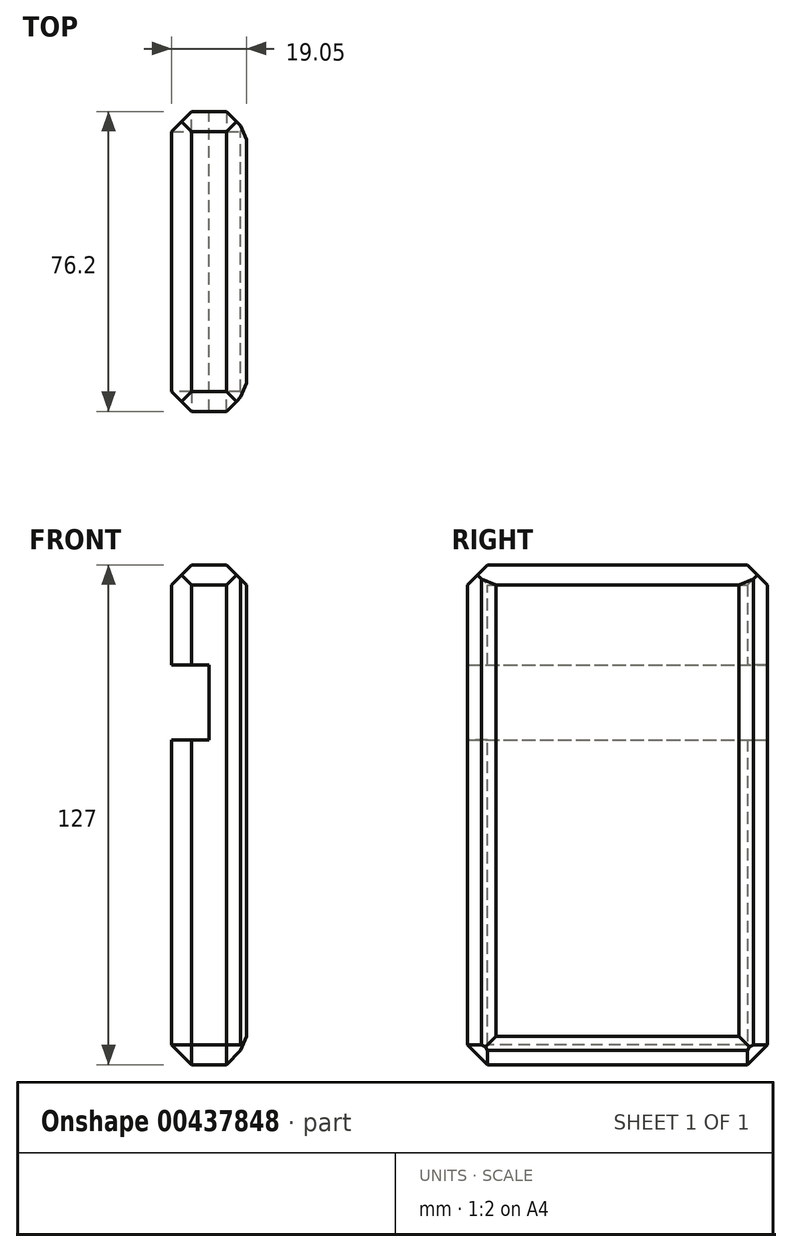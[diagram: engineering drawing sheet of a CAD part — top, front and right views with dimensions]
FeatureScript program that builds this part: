
annotation { "Feature Type Name" : "Feature", "Feature Type Description" : "" }
export const myFeature = defineFeature(function(context is Context, id is Id, definition is map)
    precondition{}
    {
        {
            var Q0;
            Q0=qCreatedBy(makeId("Front.planeOp"),FACE);
            var sketch = newSketch(context, id + "F0", { "sketchPlane" : qUnion([Q0])});
            skLineSegment(sketch, "E0", {"start": v(13.13, -19.14) * mm, "end": v(13.13, 107.86) * mm});
            skLineSegment(sketch, "E1", {"start": v(13.13, 107.86) * mm, "end": v(-5.92, 107.86) * mm});
            skLineSegment(sketch, "E2", {"start": v(-5.92, 107.86) * mm, "end": v(-5.92, 82.46) * mm});
            skLineSegment(sketch, "E3", {"start": v(-5.92, 82.46) * mm, "end": v(3.6, 82.46) * mm});
            skLineSegment(sketch, "E4", {"start": v(3.6, 82.46) * mm, "end": v(3.6, 63.41) * mm});
            skLineSegment(sketch, "E5", {"start": v(3.6, 63.41) * mm, "end": v(-5.92, 63.41) * mm});
            skLineSegment(sketch, "E6", {"start": v(-5.92, 63.41) * mm, "end": v(-5.92, -19.14) * mm});
            skLineSegment(sketch, "E7", {"start": v(-5.92, -19.14) * mm, "end": v(13.13, -19.14) * mm});
            skSolve(sketch);
        }
        {
            var Q0;
            Q0 = qSketchRegion(id + "F0", true);
            extrude(context, id + "F1", {"entities" : qUnion([Q0]), "depth" : 76.2 * mm});
        }
        {
            var Q0;
            Q0=makeQuery(id+"F1.opExtrude","CAP_EDGE",EDGE,{"disambiguationData":[OSD([sQuery(id+"F0.wireOp",EDGE,"E2")])],"isStart":true});
            var Q1;
            Q1=makeQuery(id+"F1.opExtrude","CAP_EDGE",EDGE,{"disambiguationData":[OSD([sQuery(id+"F0.wireOp",EDGE,"E0")])],"isStart":true});
            var Q2;
            Q2=makeQuery(id+"F1.opExtrude","CAP_EDGE",EDGE,{"disambiguationData":[OSD([sQuery(id+"F0.wireOp",EDGE,"E7")])],"isStart":true});
            var Q3;
            Q3=makeQuery(id+"F1.opExtrude","CAP_EDGE",EDGE,{"disambiguationData":[OSD([sQuery(id+"F0.wireOp",EDGE,"E6")])],"isStart":true});
            var Q4;
            Q4=makeQuery(id+"F1.opExtrude","SWEPT_EDGE",EDGE,{"disambiguationData":[OSD([sQuery(id+"F0.wireOp",EDGE,"E6"),sQuery(id+"F0.wireOp",EDGE,"E7")])]});
            var Q5;
            Q5=makeQuery(id+"F1.opExtrude","CAP_EDGE",EDGE,{"disambiguationData":[OSD([sQuery(id+"F0.wireOp",EDGE,"E6")])],"isStart":false});
            var Q6;
            Q6=makeQuery(id+"F1.opExtrude","SWEPT_EDGE",EDGE,{"disambiguationData":[OSD([sQuery(id+"F0.wireOp",EDGE,"E0"),sQuery(id+"F0.wireOp",EDGE,"E7")])]});
            var Q7;
            Q7=makeQuery(id+"F1.opExtrude","CAP_EDGE",EDGE,{"disambiguationData":[OSD([sQuery(id+"F0.wireOp",EDGE,"E7")])],"isStart":false});
            var Q8;
            Q8=makeQuery(id+"F1.opExtrude","CAP_EDGE",EDGE,{"disambiguationData":[OSD([sQuery(id+"F0.wireOp",EDGE,"E0")])],"isStart":false});
            var Q9;
            Q9=makeQuery(id+"F1.opExtrude","CAP_EDGE",EDGE,{"disambiguationData":[OSD([sQuery(id+"F0.wireOp",EDGE,"E1")])],"isStart":false});
            var Q10;
            Q10=makeQuery(id+"F1.opExtrude","SWEPT_EDGE",EDGE,{"disambiguationData":[OSD([sQuery(id+"F0.wireOp",EDGE,"E1"),sQuery(id+"F0.wireOp",EDGE,"E2")])]});
            chamfer(context, id + "F2", {"entities" : qUnion([Q0, Q1, Q2, Q3, Q4, Q5, Q6, Q7, Q8, Q9, Q10]), "width" : 5.08 * mm, "tangentPropagation" : true});
        }
        {
            var Q0;
            Q0=makeQuery(id+"F1.opExtrude","CAP_EDGE",EDGE,{"disambiguationData":[OSD([sQuery(id+"F0.wireOp",EDGE,"E2")])],"isStart":false});
            chamfer(context, id + "F3", {"entities" : qUnion([Q0]), "width" : 5.08 * mm, "tangentPropagation" : true});
        }
        {
            var Q0;
            Q0=makeQuery(id+"F1.opExtrude","CAP_EDGE",EDGE,{"disambiguationData":[OSD([sQuery(id+"F0.wireOp",EDGE,"E1")])],"isStart":true});
            chamfer(context, id + "F4", {"entities" : qUnion([Q0]), "width" : 5.08 * mm, "tangentPropagation" : true});
        }
        {
            var Q0;
            Q0=makeQuery(id+"F1.opExtrude","SWEPT_EDGE",EDGE,{"disambiguationData":[OSD([sQuery(id+"F0.wireOp",EDGE,"E0"),sQuery(id+"F0.wireOp",EDGE,"E1")])]});
            var Q1;
            {var subQ0=sQuery(id+"F0.wireOp",EDGE,"E0");Q1=makeQuery(id+"F2.opChamfer","BLEND_EDGE",EDGE,{"blendedFrom":[makeQuery(id+"F1.opExtrude","CAP_EDGE",EDGE,{"disambiguationData":[OSD([subQ0])],"isStart":false}),makeQuery(id+"F1.opExtrude","SWEPT_FACE",FACE,{"disambiguationData":[OSD([subQ0])]})],"blendedInto":[makeQuery(id+"F1.opExtrude","SWEPT_FACE",FACE,{"disambiguationData":[OSD([subQ0])]})]});}
            var Q2;
            {var subQ0=sQuery(id+"F0.wireOp",EDGE,"E0");Q2=makeQuery(id+"F2.opChamfer","BLEND_EDGE",EDGE,{"blendedFrom":[makeQuery(id+"F1.opExtrude","CAP_EDGE",EDGE,{"disambiguationData":[OSD([subQ0])],"isStart":true}),makeQuery(id+"F1.opExtrude","SWEPT_FACE",FACE,{"disambiguationData":[OSD([subQ0])]})],"blendedInto":[makeQuery(id+"F1.opExtrude","SWEPT_FACE",FACE,{"disambiguationData":[OSD([subQ0])]})]});}
            var Q3;
            {var subQ0=sQuery(id+"F0.wireOp",EDGE,"E0");Q3=makeQuery(id+"F2.opChamfer","BLEND_EDGE",EDGE,{"blendedFrom":[makeQuery(id+"F1.opExtrude","SWEPT_EDGE",EDGE,{"disambiguationData":[OSD([subQ0,sQuery(id+"F0.wireOp",EDGE,"E7")])]}),makeQuery(id+"F1.opExtrude","SWEPT_FACE",FACE,{"disambiguationData":[OSD([subQ0])]})],"blendedInto":[makeQuery(id+"F1.opExtrude","SWEPT_FACE",FACE,{"disambiguationData":[OSD([subQ0])]})]});}
            chamfer(context, id + "F5", {"entities" : qUnion([Q0, Q1, Q2, Q3]), "width" : 5.08 * mm, "tangentPropagation" : true});
        }
    });
